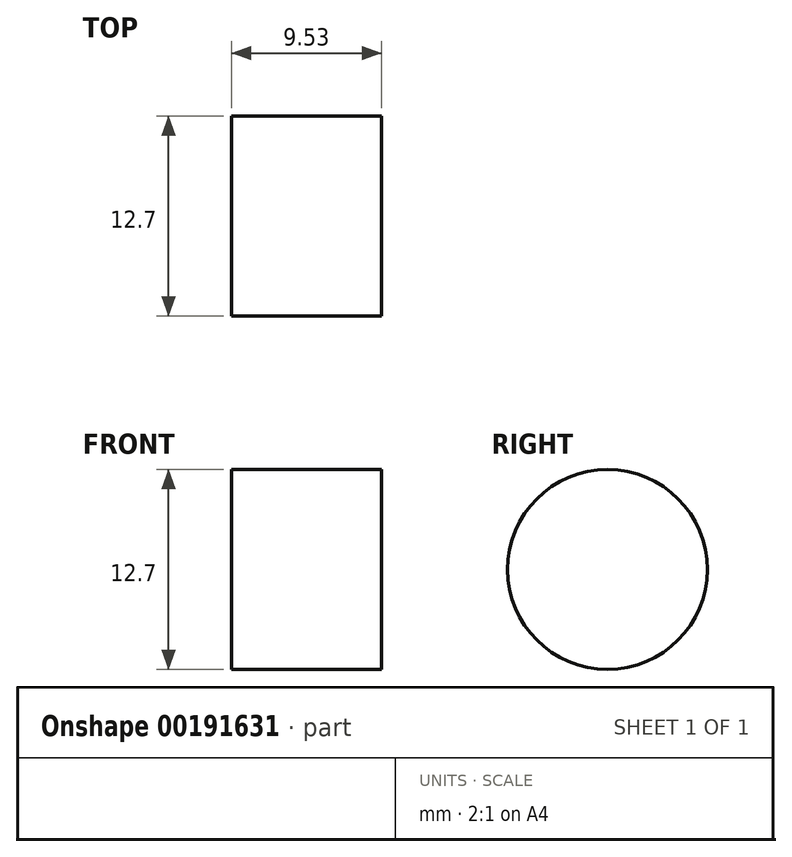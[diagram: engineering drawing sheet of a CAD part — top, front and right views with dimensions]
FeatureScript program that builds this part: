
annotation { "Feature Type Name" : "Feature", "Feature Type Description" : "" }
export const myFeature = defineFeature(function(context is Context, id is Id, definition is map)
    precondition{}
    {
        {
            var Q0;
            Q0=qCreatedBy(makeId("Right.planeOp"),FACE);
            var sketch = newSketch(context, id + "F0", { "sketchPlane" : qUnion([Q0])});
            skCircle(sketch, "E0", {"center": v(0, 0) * mm, "radius": 6.35 * mm});
            skSolve(sketch);
        }
        {
            var Q0;
            Q0=makeQuery(id+"F0.imprint","IMPRINT",FACE,{"disambiguationData":[TD([[makeQuery(id+"F0.imprint","IMPRINT",EDGE,{"derivedFrom":sQuery(id+"F0.wireOp",EDGE,"E0")}),1.0]])]});
            extrude(context, id + "F1", {"entities" : qUnion([Q0]), "depth" : 9.52 * mm});
        }
    });
